# Revit family: PRD_FrankeWS_WshBsnsWsts_RondoWasteValve_E-XINH-VALVE,SS
name_source: partatom
category: Plumbing Fixtures
revit_build: Autodesk Revit 2018 (Build: 20190510_1515(x64)
units: mm (PartAtom-declared; Revit-internal decimal feet)

## family parameters
Always vertical = Yes
Cut with Voids When Loaded = No
OmniClass Number = 23.45.00.00
OmniClass Title = Sanitary, Laundry, and Cleaning Equipment
Part Type = Normal
Room Calculation Point = No
Round Connector Dimension = Use Diameter
Shared = No
Work Plane-Based = No

## types (2) — shared parameters
AssetType = Fixed
Category = Pr_70_55_96_97, Wash basins wastes
DurationUnit = year
Features = Waste valve
IfcExportAs = IfcWasteTerminalType
IfcExportType = WASTETRAP
Manufacturer = KWC Group AG
ManufacturerName = KWC Group AG
ManufacturerURL = www.kwc.com
NBSDescription = Wastes for wash basins
NBSReference = 45-35-70/372
OutletConnectionSize = 32 mm  [stored 0.104987 ft]
ProductInformation = https://pim.kwc.com
Shape = Cylindrical
Size = DN 32 (1 1/4 inch.)
URL = www.kwc.com
Uniclass2015Code = Pr_70_55_96_97
Uniclass2015Title = Wash basins wastes
Uniclass2015Version = Products v1.10
Version = 1
WarrantyDurationUnit = year
WasteSize = 32  [stored 0.104987 ft]
WasteTrapType = Other
WasteValveMaterial = PRD_AR_ChromatedBrass_HighPolished
zero-valued in all types: InletConnectionSize, NominalHeight, NominalLength, NominalWidth

## per-type parameters (varying)
| type | BIMObjectName | Description | GrossWeight | ModelNumber | Name | NetWeight |
| E-XINH-VALVE-SS | PRD_AR_WashBasinsWastes_RondoWasteValve_E-XINH-VALVE-SS | Dome waste outlet DN32, chromated brass , lockable, only applicable for washbasins with overflow. | 1.00 kg | 2000101361 | RONDO waste valve E-XINH-VALVE-SS | 1.00 kg |
| E-XINH-VALVE | PRD_AR_WashBasinsWastes_RondoWasteValve_E-XINH-VALVE | Dome waste outlet DN 32, chromated brass, only applicable for washbasins with overflow. | 0.32 kg | 2000101365 | RONDO waste valve E-XINH-VALVE | 0.32 kg |

note: column(s) folded — value = type name in every type: Model, ModelReference

note: [stored X ft] marks values corroborated as IEEE doubles in the binary element streams (Revit-internal decimal feet)

## geometry (parser evidence)
native form markers: Sweep x2
no freeform markers — native parametric forms only
